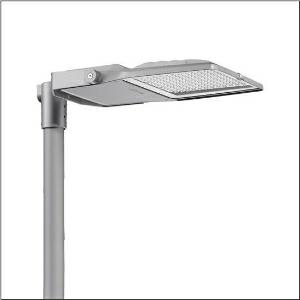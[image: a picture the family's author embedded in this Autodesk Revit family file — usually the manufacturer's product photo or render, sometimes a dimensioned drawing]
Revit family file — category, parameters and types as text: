
# Revit family: floodlight_fl_21_iq_midi___pl33t_5xa7781e6f3a_cd97
name_source: partatom
category: Lighting Fixtures
units: mm (PartAtom-declared; Revit-internal decimal feet)

## family parameters
Cut with Voids When Loaded = No
Host = Face
Light Source = No
Part Type = Normal
Room Calculation Point = No
Round Connector Dimension = Use Diameter
Shared = No

## types (1)
- --- (1 x LED, 21270 lm, 208.1 W, 5700K)
    Apparent Load = 208 VA
    CIE Flux Codes = 26 75 99 100 100
    Color Rendering = 90
    Color Temperature = 5700K
    Default Elevation = 1800 mm
    Description = Floodlight FL 21 iQ midi, floodlight, primary light control with lens, of PMMA, primary optical cover: protective disc, of toughened safety glass, transparent, light distribution: PL33T, light emission: direct distribution, installation type: surface-mounted, LED, High Power LED, rated luminous flux: 21.270lm, luminous efficacy: 102lm/W, light colour: 957, colour temperature: 5700K, control gear: iQ Comfort/DALI, control: optimised constant luminous flux control (CLO 2.0), Desk-Remote (wireless, voltage-free reading and setting of iQ features in the workshop via application-optimized NFC function/RFID function), Light-Fading, Smart-Wire, Night-Set, Lumen-Switch, Temp-Guard, Auto-Match, with terminal, 6-pole, mains connection: 220..240V, AC, 50/60Hz, start of lifetime: 208W, end of service life: 227W, reduction: 90W, luminaire housing, of diecast aluminium, powder-coated, Siteco® metallic grey (DB 702S), corrosivity category C5 mid according to DIN EN ISO 12944, suitable for swimming pools, chlorine-resistant, sealing non-destructively replaceable, please order mast flange separately, mast bracket, of steel, galvanised, powder-coated, Siteco® metallic grey (DB 702S), protection rating (complete): IP66, insulation class (complete): insulation class II (safety insulation), certification: CE, ENEC, VDE, protection symbol: D, impact resistance: IK08, permissible operating ambient temperature: -40..+40°C, permissible operating ambient temperature for outdoor applications: -40..+50°C, standard: DIN EN 12944, LABS conformity tested according to VDMA 24364:2018-05, packaging unit: 1 piece

Light Distribution: PL33T
    Height = 76 mm
    Lamp = 1 x LED
    Lamp Light Flux = 21270 lm
    Lamp Power = 208.1 W
    Lamp count = 1
    Length = 657 mm
    Luminous efficacy = 102 lm/W
    Manufacturer = Siteco
    ModVariant = No
    Model = 5XA7781E6F3A
    Number of Poles = 1
    OnlyDefault = Yes
    Power Factor = 1
    Product Name = Floodlight FL 21 iQ midi | PL33T
    Product group = floodlight | pylon annexe
    ProductGroupID = 6201
    Protection Class = Protection class II
    Protection Degree = IP 66
    RLX_Detail_Level = 1
    RLX_Emergency_Light_Flux = 0 lm
    RLX_Emergency_Type = 0
    RLX_Emergency_Type_DB = No
    RlxData = <blob elided: 153829 chars, md5=027ffe6a>
    Socket = socket
    Standby Power = 0 W
    System Light Flux = 21270 lm
    System Power = 208 W
    Type Comments = factory setting: luminous flux: 100 % | dim-lin: 254 | 710 mA
    Type Image = l_1007123.jpg
    URL = http://relux.com
    VarID = @adj_125073
    Voltage = 0 V
    Weight = 0.00 kg
    Width = 442 mm

## geometry (parser evidence)
native form markers: Blend x4, Sweep x13
no freeform markers — native parametric forms only
